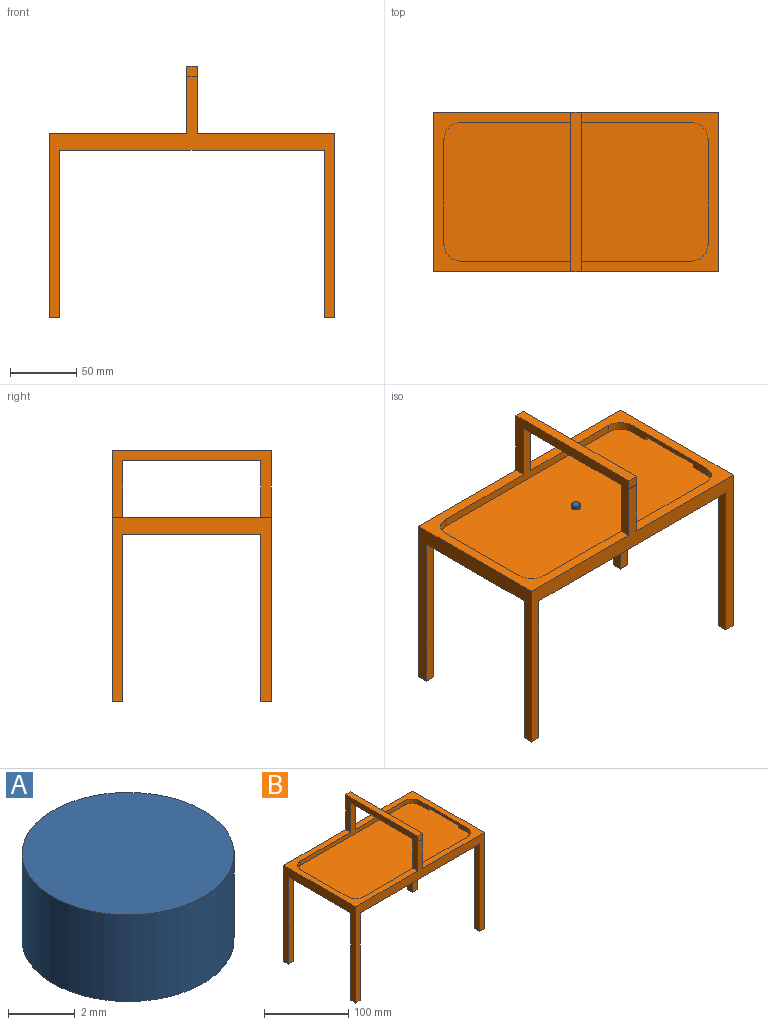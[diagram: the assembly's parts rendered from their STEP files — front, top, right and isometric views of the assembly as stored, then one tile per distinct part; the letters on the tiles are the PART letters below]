
ASSEMBLY  parts=2 mates=1
PART A: 3 faces, bbox 6.4x6.4x3.2 mm
  f0: cylinder r=3.17mm len=6.35mm, axis (0,0,-1), area 63.3mm2, adj f1,f2
  f1: plane 6.35x6.35mm, normal (0,0,1), area 31.7mm2, adj f0
  f2: plane 6.35x6.35mm, normal (0,0,-1), area 31.7mm2, adj f0
PART B: 42 faces, bbox 215.9x121x190.5 mm
  f0: plane 79.38x6.35mm, normal (1,0,0), area 362.9mm2, adj f5,f8,f9,f15,f34,f35,f36
  f1: plane 174.63x49.2mm, normal (0,-1,0), area 1449.5mm2, adj f4,f5,f9,f10,f15,f28,f29,f33
  f2: plane 174.63x49.2mm, normal (0,1,0), area 1449.5mm2, adj f4,f5,f8,f11,f15,f28,f29,f33
  f3: plane 215.9x182.55mm, normal (0,-1,0), area 5098.7mm2, adj f4,f5,f6,f12,f13,f16,f18,f26
  f4: plane 120.65x103.98mm, normal (0,0,1), area 2551.5mm2, adj f1,f2,f3,f7,f10,f11,f13,f14
  f5: plane 120.65x103.98mm, normal (0,0,1), area 2551.5mm2, adj f0,f1,f2,f3,f8,f9,f12,f14
  f6: plane 215.9x120.65mm, normal (0,0,-1), area 25796.3mm2, adj f3,f12,f13,f14,f16,f17,f19,f20
  f7: plane 79.38x6.35mm, normal (-1,0,0), area 342.7mm2, adj f4,f10,f11,f15,f38,f39,f40
  f8: cylinder r=12.7mm len=12.7mm, axis (0,0,-1), area 126.7mm2, adj f0,f2,f5,f15
  f9: cylinder r=12.7mm len=12.7mm, axis (0,0,-1), area 126.7mm2, adj f0,f1,f5,f15
  f10: cylinder r=12.7mm len=12.7mm, axis (0,0,-1), area 126.7mm2, adj f1,f4,f7,f15
  f11: cylinder r=12.7mm len=12.7mm, axis (0,0,-1), area 126.7mm2, adj f2,f4,f7,f15
  f12: plane 139.7x120.65mm, normal (-1,0,0), area 3548.4mm2, adj f3,f5,f6,f14,f17,f18,f19,f21
  f13: plane 139.7x120.65mm, normal (1,0,0), area 3548.4mm2, adj f3,f4,f6,f14,f22,f24,f25,f27
  f14: plane 215.9x190.5mm, normal (0,1,0), area 5161.9mm2, adj f4,f5,f6,f12,f13,f20,f21,f23
  f15: plane 209.55x104.78mm, normal (0,0,1), area 21262.7mm2, adj f0,f1,f2,f7,f8,f9,f10,f11
  f16: plane 127x7.94mm, normal (1,0,0), area 1008.1mm2, adj f3,f6,f17,f18
  f17: plane 127x7.94mm, normal (0,1,0), area 1008.1mm2, adj f6,f12,f16,f18
  f18: plane 7.94x7.94mm, normal (0,0,-1), area 63mm2, adj f3,f12,f16,f17
  f19: plane 127x7.94mm, normal (0,-1,0), area 1008.1mm2, adj f6,f12,f20,f21
  f20: plane 127x7.94mm, normal (1,0,0), area 1008.1mm2, adj f6,f14,f19,f21
  f21: plane 7.94x7.94mm, normal (0,0,-1), area 63mm2, adj f12,f14,f19,f20
  f22: plane 127x7.94mm, normal (0,-1,0), area 1008.1mm2, adj f6,f13,f23,f24
  f23: plane 127x7.94mm, normal (-1,0,0), area 1008.1mm2, adj f6,f14,f22,f24
  f24: plane 7.94x7.94mm, normal (0,0,-1), area 63mm2, adj f13,f14,f22,f23
  f25: plane 127x7.94mm, normal (0,1,0), area 1008.1mm2, adj f6,f13,f26,f27
  f26: plane 127x7.94mm, normal (-1,0,0), area 1008.1mm2, adj f3,f6,f25,f27
  f27: plane 7.94x7.94mm, normal (0,0,-1), area 63mm2, adj f3,f13,f25,f26
  f28: plane 120.97x50.8mm, normal (-1,0,0), area 1642mm2, adj f1,f2,f3,f5,f14,f30,f31,f32
  f29: plane 120.97x50.8mm, normal (1,0,0), area 1642mm2, adj f1,f2,f3,f4,f14,f30,f31,f32
  f30: plane 120.97x7.95mm, normal (0,0,1), area 961.7mm2, adj f14,f28,f29,f31
  f31: plane 7.95x7.95mm, normal (0,-1,0), area 63.2mm2, adj f28,f29,f30,f32
  f32: plane 7.95x0.32mm, normal (0,0,-1), area 2.5mm2, adj f3,f28,f29,f31
  f33: plane 104.78x7.95mm, normal (0,0,-1), area 833mm2, adj f1,f2,f28,f29
  f34: plane 6.35x3.18mm, normal (0,-1,0), area 20.2mm2, adj f0,f15,f35,f37
  f35: plane 44.45x6.35mm, normal (0,0,-1), area 282.3mm2, adj f0,f34,f36,f37
  f36: plane 6.35x3.18mm, normal (0,1,0), area 20.2mm2, adj f0,f15,f35,f37
  f37: plane 44.45x3.18mm, normal (1,0,0), area 141.1mm2, adj f15,f34,f35,f36
  f38: plane 3.18x3.18mm, normal (0,1,0), area 10.1mm2, adj f7,f15,f39,f41
  f39: plane 50.8x3.18mm, normal (0,0,-1), area 161.3mm2, adj f7,f38,f40,f41
  f40: plane 3.18x3.18mm, normal (0,-1,0), area 10.1mm2, adj f7,f15,f39,f41
  f41: plane 50.8x3.18mm, normal (-1,0,0), area 161.3mm2, adj f15,f38,f39,f40
PLACE A rot(axis=(0,0,1),0deg) t=(-207.65,13.49,-14.1)mm
PLACE B t=(-207.65,13.49,-20.45)mm
MATE planar A.f0 <-> B.f15  axis (0,0,-1) through (-207.65,13.49,-14.1)mm
